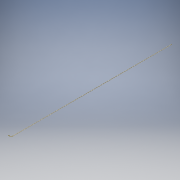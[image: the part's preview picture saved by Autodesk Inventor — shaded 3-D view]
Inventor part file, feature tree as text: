
AUTODESK INVENTOR PART (.ipt)
format: ipt  version: 2018 (Build 220112000, 112)  size: 104,960 bytes
history: native  units: mm
features: sketch x2, sweep x1
ambient origin geometry x8: Origin, YZ Plane, XZ Plane, XY Plane, X Axis, Y Axis, Z Axis, Center Point
bodies: Body1 (feature_tree)
feature tree (3):
  sweep  "Sweep2"
  sketch  "Sketch1"  dims[d0=1.0mm d1=2.0mm]
  sketch  "Sketch3"  dims[d2=1.5mm d7=0.5mm d8=0.0mm d9=0.0mm d18=169.0mm]
